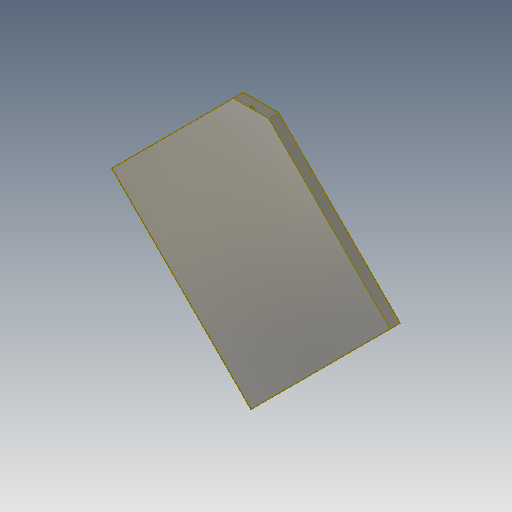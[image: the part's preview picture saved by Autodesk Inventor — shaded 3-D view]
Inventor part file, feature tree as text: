
AUTODESK INVENTOR PART (.ipt)
format: ipt  version: 2020 (Build 240168000, 168)  size: 132,608 bytes
history: native  units: mm
features: extrude x3, sketch x3, mirror x1
ambient origin geometry x8: Origin, YZ Plane, XZ Plane, XY Plane, X Axis, Y Axis, Z Axis, Center Point
bodies: Solid1 (feature_tree)
feature tree (7):
  extrude  "Extrusion1"  Depth=200.0mm
  extrude  "Extrusion3"  TaperAngle=0.0deg  [1 undecoded]
  extrude  "Extrusion2"  Depth=2.0mm
  mirror  "Mirror1"
  sketch  "Sketch1"  dims[d0=200.0mm d1=200.0mm]
  sketch  "Sketch2"  dims[d3=10.0mm d4=0.0mm]
  sketch  "Sketch4"  dims[d5=0.2mm d6=0.0mm d7=25.4mm d8=25.4mm d9=0.2mm d14=10.0mm d15=0.0mm d16=4.0mm d17=2.0mm]
note: 1 required parameter value undecoded (feature->parameter linkage not recoverable at this tier; creation-order binding heuristic only, values carry confidence <= 0.55)
